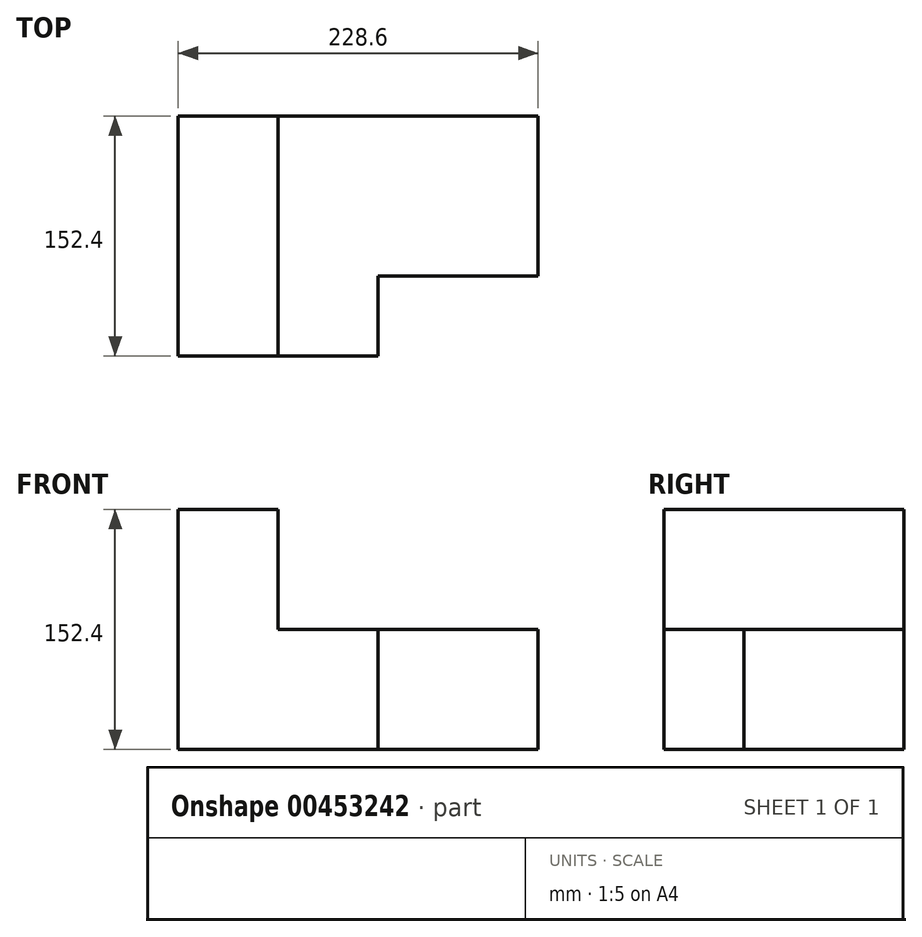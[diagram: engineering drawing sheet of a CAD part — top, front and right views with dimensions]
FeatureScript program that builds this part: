
annotation { "Feature Type Name" : "Feature", "Feature Type Description" : "" }
export const myFeature = defineFeature(function(context is Context, id is Id, definition is map)
    precondition{}
    {
        {
            var Q0;
            Q0=qCreatedBy(makeId("Front.planeOp"),FACE);
            var sketch = newSketch(context, id + "F0", { "sketchPlane" : qUnion([Q0])});
            skLineSegment(sketch, "E0", {"start": v(114.3, -76.2) * mm, "end": v(-114.3, -76.2) * mm});
            skLineSegment(sketch, "E1", {"start": v(-114.3, -76.2) * mm, "end": v(-114.3, 76.2) * mm});
            skLineSegment(sketch, "E2.MirrorCS", {"start": v(114.3, -76.2) * mm, "end": v(114.3, 76.2) * mm});
            skLineSegment(sketch, "E3.MirrorCS", {"start": v(114.3, 76.2) * mm, "end": v(-114.3, 76.2) * mm});
            skSolve(sketch);
        }
        {
            var Q0;
            Q0=makeQuery(id+"F0.imprint","IMPRINT",FACE,{"disambiguationData":[TD([[makeQuery(id+"F0.imprint","IMPRINT",EDGE,{"derivedFrom":sQuery(id+"F0.wireOp",EDGE,"E0")}),-1.0]])]});
            extrude(context, id + "F1", {"entities" : qUnion([Q0]), "endBound" : BoundingType.SYMMETRIC, "depth" : 152.4 * mm});
        }
        {
            var Q0;
            Q0=makeQuery(id+"F1.opExtrude","CAP_FACE",FACE,{"disambiguationData":[OSD([sQuery(id+"F0.wireOp",EDGE,"E0"),sQuery(id+"F0.wireOp",EDGE,"E1"),sQuery(id+"F0.wireOp",EDGE,"E2.MirrorCS"),sQuery(id+"F0.wireOp",EDGE,"E3.MirrorCS")])],"isStart":false});
            var sketch = newSketch(context, id + "F2", { "sketchPlane" : qUnion([Q0])});
            skLineSegment(sketch, "E4", {"start": v(114.3, 76.2) * mm, "end": v(-50.8, 76.2) * mm});
            skLineSegment(sketch, "E5", {"start": v(-50.8, 76.2) * mm, "end": v(-50.8, 0) * mm});
            skLineSegment(sketch, "E6", {"start": v(-50.8, 0) * mm, "end": v(114.3, 0) * mm});
            skLineSegment(sketch, "E7", {"start": v(114.3, 0) * mm, "end": v(114.3, 76.2) * mm});
            skSolve(sketch);
        }
        {
            var Q0;
            Q0=makeQuery(id+"F2.imprint","IMPRINT",FACE,{"disambiguationData":[TD([[makeQuery(id+"F2.imprint","IMPRINT",EDGE,{"derivedFrom":sQuery(id+"F2.wireOp",EDGE,"E4")}),1.0]])]});
            extrude(context, id + "F3", {"entities" : qUnion([Q0]), "operationType" : NewBodyOperationType.REMOVE, "endBound" : BoundingType.THROUGH_ALL, "oppositeDirection" : true, "depth" : 25.4 * mm});
        }
        {
            var Q0;
            Q0=makeQuery(id+"F1.opExtrude","CAP_FACE",FACE,{"disambiguationData":[OSD([sQuery(id+"F0.wireOp",EDGE,"E0"),sQuery(id+"F0.wireOp",EDGE,"E1"),sQuery(id+"F0.wireOp",EDGE,"E2.MirrorCS"),sQuery(id+"F0.wireOp",EDGE,"E3.MirrorCS")])],"isStart":false});
            var sketch = newSketch(context, id + "F4", { "sketchPlane" : qUnion([Q0])});
            skLineSegment(sketch, "E8", {"start": v(114.3, -76.2) * mm, "end": v(12.7, -76.2) * mm});
            skLineSegment(sketch, "E9", {"start": v(12.7, -76.2) * mm, "end": v(12.7, 0) * mm});
            skLineSegment(sketch, "E10", {"start": v(12.7, 0) * mm, "end": v(114.3, 0) * mm});
            skLineSegment(sketch, "E11", {"start": v(114.3, 0) * mm, "end": v(114.3, -76.2) * mm});
            skSolve(sketch);
        }
        {
            var Q0;
            Q0=makeQuery(id+"F4.imprint","IMPRINT",FACE,{"disambiguationData":[TD([[makeQuery(id+"F4.imprint","IMPRINT",EDGE,{"derivedFrom":sQuery(id+"F4.wireOp",EDGE,"E8")}),-1.0]])]});
            extrude(context, id + "F5", {"entities" : qUnion([Q0]), "operationType" : NewBodyOperationType.REMOVE, "oppositeDirection" : true, "depth" : 50.8 * mm});
        }
    });
